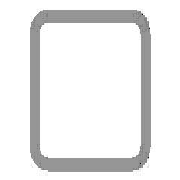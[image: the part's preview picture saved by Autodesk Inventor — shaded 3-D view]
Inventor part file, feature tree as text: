
AUTODESK INVENTOR PART (.ipt)
format: ipt  version: 2024 (Build 280153000, 153)  size: 129,024 bytes
history: native  units: mm (DEFAULTED — no unit token found)
features: other x4, extrude x1, sketch x1, plane x1
ambient origin geometry x8: Origin, YZ Plane, XZ Plane, XY Plane, X Axis, Y Axis, Z Axis, Center Point
bodies: Solid1 (feature_tree)
feature tree (7):
  parser-record x1  (decoder bookkeeping rows leaked as tree rows — omitted from the tree; the rows remain in map.json)
  other  "Driven Length"
  other  "Plano inicial"
  other  "Plano final"
  extrude  "Cuerpo"  TaperAngle=0.0deg  [1 undecoded]
  sketch  "Sketch3"  dims[d3=200.0mm d4=0.0mm d10=50.8mm d11=50.8mm d12=3.175mm d13=-0.0mm d14=200.0mm d15=25.4mm d16=25.4mm d17=6.35mm d18=90.0deg d19=200.0mm]
  plane  "Work Plane3"
note: 1 required parameter value undecoded (feature->parameter linkage not recoverable at this tier; creation-order binding heuristic only, values carry confidence <= 0.55)
